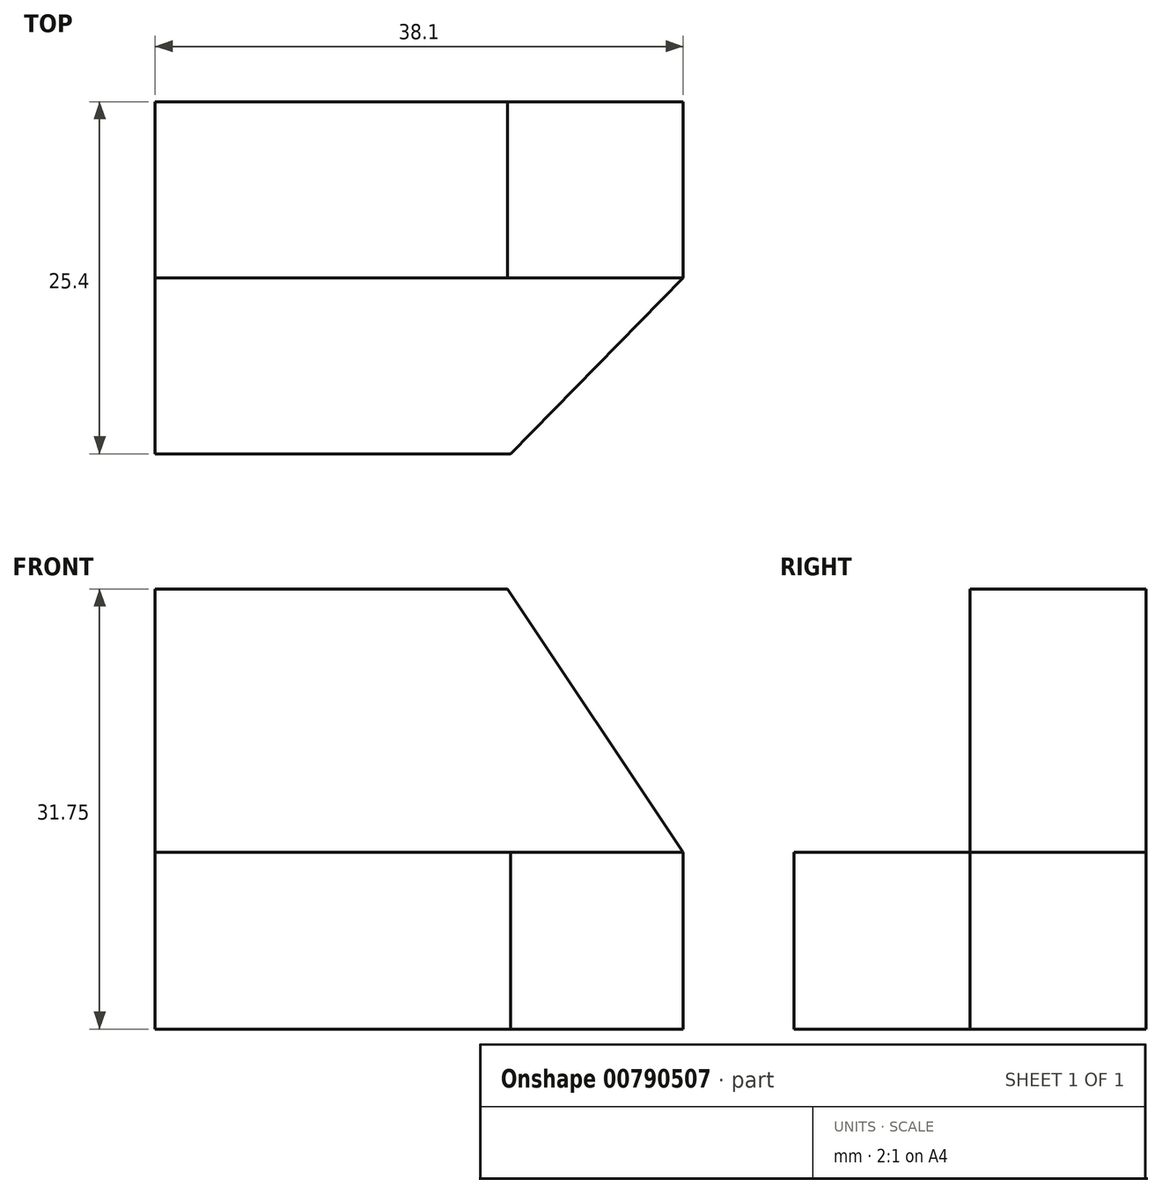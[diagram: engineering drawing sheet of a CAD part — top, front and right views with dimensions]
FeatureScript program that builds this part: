
annotation { "Feature Type Name" : "Feature", "Feature Type Description" : "" }
export const myFeature = defineFeature(function(context is Context, id is Id, definition is map)
    precondition{}
    {
        {
            var Q0;
            Q0=qCreatedBy(makeId("Front.planeOp"),FACE);
            var sketch = newSketch(context, id + "F0", { "sketchPlane" : qUnion([Q0])});
            skLineSegment(sketch, "E0", {"start": v(0, 31.75) * mm, "end": v(0, 0) * mm});
            skLineSegment(sketch, "E1", {"start": v(0, 0) * mm, "end": v(38.1, 0) * mm});
            skLineSegment(sketch, "E2", {"start": v(38.1, 0) * mm, "end": v(38.1, 31.75) * mm});
            skLineSegment(sketch, "E3", {"start": v(38.1, 31.75) * mm, "end": v(0, 31.75) * mm});
            skSolve(sketch);
        }
        {
            var Q0;
            Q0=makeQuery(id+"F0.imprint","IMPRINT",FACE,{"disambiguationData":[TD([[makeQuery(id+"F0.imprint","IMPRINT",EDGE,{"derivedFrom":sQuery(id+"F0.wireOp",EDGE,"E0")}),1.0]])]});
            extrude(context, id + "F1", {"entities" : qUnion([Q0]), "depth" : 25.4 * mm, "offsetDistance" : 25.4 * mm});
        }
        {
            var Q0;
            Q0=makeQuery(id+"F1.opExtrude","CAP_FACE",FACE,{"disambiguationData":[OSD([sQuery(id+"F0.wireOp",EDGE,"E0"),sQuery(id+"F0.wireOp",EDGE,"E1"),sQuery(id+"F0.wireOp",EDGE,"E2"),sQuery(id+"F0.wireOp",EDGE,"E3")])],"isStart":false});
            var sketch = newSketch(context, id + "F2", { "sketchPlane" : qUnion([Q0])});
            skLineSegment(sketch, "E4", {"start": v(38.1, 0) * mm, "end": v(38.1, 12.77) * mm});
            skLineSegment(sketch, "E5", {"start": v(0, 31.75) * mm, "end": v(25.43, 31.75) * mm});
            skLineSegment(sketch, "E6", {"start": v(25.43, 31.75) * mm, "end": v(38.1, 12.77) * mm});
            skSolve(sketch);
        }
        {
            var Q0;
            {var subQ0=sQuery(id+"F2.wireOp",EDGE,"E6");Q0=makeQuery(id+"F2.imprint","IMPRINT",FACE,{"disambiguationData":[TD([[makeQuery(id+"F2.imprint","IMPRINT",EDGE,{"derivedFrom":subQ0}),1.0]])]});}
            extrude(context, id + "F3", {"entities" : qUnion([Q0]), "operationType" : NewBodyOperationType.REMOVE, "endBound" : BoundingType.THROUGH_ALL, "oppositeDirection" : true, "depth" : 25.4 * mm, "offsetDistance" : 25.4 * mm});
        }
        {
            var Q0;
            Q0=makeQuery(id+"F1.opExtrude","CAP_FACE",FACE,{"disambiguationData":[OSD([sQuery(id+"F0.wireOp",EDGE,"E0"),sQuery(id+"F0.wireOp",EDGE,"E1"),sQuery(id+"F0.wireOp",EDGE,"E2"),sQuery(id+"F0.wireOp",EDGE,"E3")])],"isStart":false});
            var sketch = newSketch(context, id + "F4", { "sketchPlane" : qUnion([Q0])});
            skLineSegment(sketch, "E7", {"start": v(38.1, 12.77) * mm, "end": v(0, 12.77) * mm});
            skPoint(sketch, "E7.endSnap0", {"position": v(0, 15.88) * mm});
            skSolve(sketch);
        }
        {
            var Q0;
            {var subQ0=sQuery(id+"F4.wireOp",EDGE,"E7");Q0=makeQuery(id+"F4.imprint","IMPRINT",FACE,{"disambiguationData":[TD([[makeQuery(id+"F4.imprint","IMPRINT",EDGE,{"derivedFrom":subQ0}),-1.0]])]});}
            extrude(context, id + "F5", {"entities" : qUnion([Q0]), "operationType" : NewBodyOperationType.REMOVE, "oppositeDirection" : true, "depth" : 12.7 * mm, "offsetDistance" : 25.4 * mm});
        }
        {
            var Q0;
            Q0=makeQuery(id+"F5.boolean.opBoolean","COPY",FACE,{"derivedFrom":makeQuery(id+"F5.opExtrude","SWEPT_FACE",FACE,{"disambiguationData":[OSD([sQuery(id+"F4.wireOp",EDGE,"E7")])]})});
            var sketch = newSketch(context, id + "F6", { "sketchPlane" : qUnion([Q0])});
            skLineSegment(sketch, "E8", {"start": v(0, -25.4) * mm, "end": v(25.63, -25.4) * mm});
            skLineSegment(sketch, "E9", {"start": v(25.63, -25.4) * mm, "end": v(38.1, -12.7) * mm});
            skSolve(sketch);
        }
        {
            var Q0;
            Q0=qSketchRegion(id+"F6",true);
            var Q1;
            {var subQ0=sQuery(id+"F6.wireOp",EDGE,"E9");Q1=makeQuery(id+"F6.imprint","IMPRINT",FACE,{"disambiguationData":[TD([[makeQuery(id+"F6.imprint","IMPRINT",EDGE,{"derivedFrom":subQ0}),-1.0]])]});}
            extrude(context, id + "F7", {"entities" : qUnion([Q0, Q1]), "operationType" : NewBodyOperationType.REMOVE, "endBound" : BoundingType.THROUGH_ALL, "oppositeDirection" : true, "depth" : 25.4 * mm, "offsetDistance" : 25.4 * mm});
        }
    });
